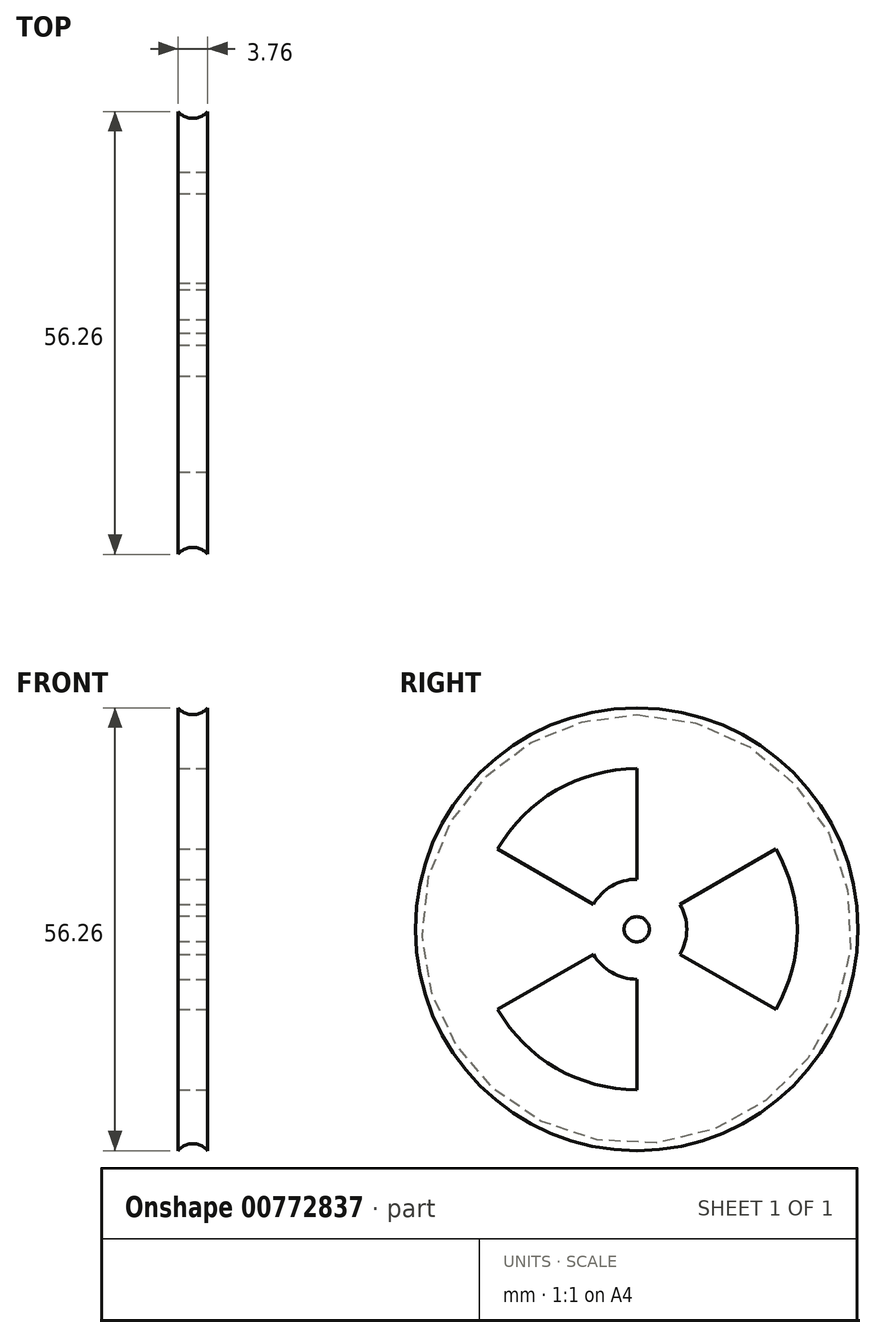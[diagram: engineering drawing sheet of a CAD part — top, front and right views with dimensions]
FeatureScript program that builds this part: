
annotation { "Feature Type Name" : "Feature", "Feature Type Description" : "" }
export const myFeature = defineFeature(function(context is Context, id is Id, definition is map)
    precondition{}
    {
        {
            var Q0;
            Q0=qCreatedBy(makeId("Front.planeOp"),FACE);
            var sketch = newSketch(context, id + "F0", { "sketchPlane" : qUnion([Q0])});
            skLineSegment(sketch, "E0.bottom", {"start": v(0, 0) * mm, "end": v(3.76, 0) * mm});
            skLineSegment(sketch, "E0.left", {"start": v(0, 0) * mm, "end": v(0, 28.13) * mm});
            skLineSegment(sketch, "E0.right", {"start": v(3.76, 0) * mm, "end": v(3.76, 28.13) * mm});
            skArc(sketch, "E1", {"start": v(0, 28.12) * mm, "mid": v(1.88, 27.25) * mm, "end": v(3.76, 28.13) * mm});
            skSolve(sketch);
        }
        {
            var Q0;
            Q0=makeQuery(id+"F0.imprint","IMPRINT",FACE,{"disambiguationData":[TD([[makeQuery(id+"F0.imprint","IMPRINT",EDGE,{"derivedFrom":sQuery(id+"F0.wireOp",EDGE,"E0.bottom")}),1.0]])]});
            var Q1;
            Q1=sQuery(id+"F0.wireOp",EDGE,"E0.bottom");
            revolve(context, id + "F1", {"surfaceOperationType" : NewSurfaceOperationType.NEW, "entities" : qUnion([Q0]), "axis" : qUnion([Q1]), "revolveType" : RevolveType.FULL});
        }
        {
            var Q0;
            Q0=qCreatedBy(makeId("Right.planeOp"),FACE);
            var sketch = newSketch(context, id + "F2", { "sketchPlane" : qUnion([Q0])});
            skCircle(sketch, "E2", {"center": v(0, 0) * mm, "radius": 6.35 * mm});
            skCircle(sketch, "E3", {"center": v(0, 0) * mm, "radius": 20.4 * mm});
            skLineSegment(sketch, "E4", {"start": v(0, 6.35) * mm, "end": v(0, 20.4) * mm});
            skLineSegment(sketch, "E5", {"start": v(0, -6.35) * mm, "end": v(0, -20.4) * mm});
            skLineSegment(sketch, "E6", {"start": v(5.5, 3.18) * mm, "end": v(17.66, 10.2) * mm});
            skLineSegment(sketch, "E7", {"start": v(-5.5, -3.18) * mm, "end": v(-17.66, -10.2) * mm});
            skLineSegment(sketch, "E8", {"start": v(-5.5, 3.17) * mm, "end": v(-17.66, 10.2) * mm});
            skLineSegment(sketch, "E9", {"start": v(5.5, -3.17) * mm, "end": v(17.66, -10.2) * mm});
            skSolve(sketch);
        }
        {
            var Q0;
            {var subQ0=sQuery(id+"F2.wireOp",EDGE,"E4");Q0=makeQuery(id+"F2.imprint","IMPRINT",FACE,{"disambiguationData":[TD([[makeQuery(id+"F2.imprint","IMPRINT",EDGE,{"derivedFrom":subQ0}),1.0]])]});}
            var Q1;
            {var subQ0=sQuery(id+"F2.wireOp",EDGE,"E5");Q1=makeQuery(id+"F2.imprint","IMPRINT",FACE,{"disambiguationData":[TD([[makeQuery(id+"F2.imprint","IMPRINT",EDGE,{"derivedFrom":subQ0}),-1.0]])]});}
            var Q2;
            {var subQ0=sQuery(id+"F2.wireOp",EDGE,"E6");Q2=makeQuery(id+"F2.imprint","IMPRINT",FACE,{"disambiguationData":[TD([[makeQuery(id+"F2.imprint","IMPRINT",EDGE,{"derivedFrom":subQ0}),-1.0]])]});}
            extrude(context, id + "F3", {"entities" : qUnion([Q0, Q1, Q2]), "operationType" : NewBodyOperationType.REMOVE, "endBound" : BoundingType.THROUGH_ALL, "oppositeDirection" : true, "depth" : 25.4 * mm, "offsetDistance" : 25.4 * mm, "hasSecondDirection" : true, "secondDirectionOppositeDirection" : false, "secondDirectionDepth" : 25.4 * mm});
        }
        {
            var Q0;
            Q0=makeQuery(id+"F1.opRevolve","SWEPT_FACE",FACE,{"disambiguationData":[OSD([sQuery(id+"F0.wireOp",EDGE,"E0.left")])]});
            var sketch = newSketch(context, id + "F4", { "sketchPlane" : qUnion([Q0])});
            skCircle(sketch, "E10", {"center": v(0, 0) * mm, "radius": 1.6 * mm});
            skSolve(sketch);
        }
        {
            var Q0;
            Q0=makeQuery(id+"F4.imprint","IMPRINT",FACE,{"disambiguationData":[TD([[makeQuery(id+"F4.imprint","IMPRINT",EDGE,{"derivedFrom":sQuery(id+"F4.wireOp",EDGE,"E10")}),1.0]])]});
            extrude(context, id + "F5", {"entities" : qUnion([Q0]), "operationType" : NewBodyOperationType.REMOVE, "endBound" : BoundingType.THROUGH_ALL, "oppositeDirection" : true, "depth" : 25.4 * mm, "offsetDistance" : 25.4 * mm});
        }
    });
